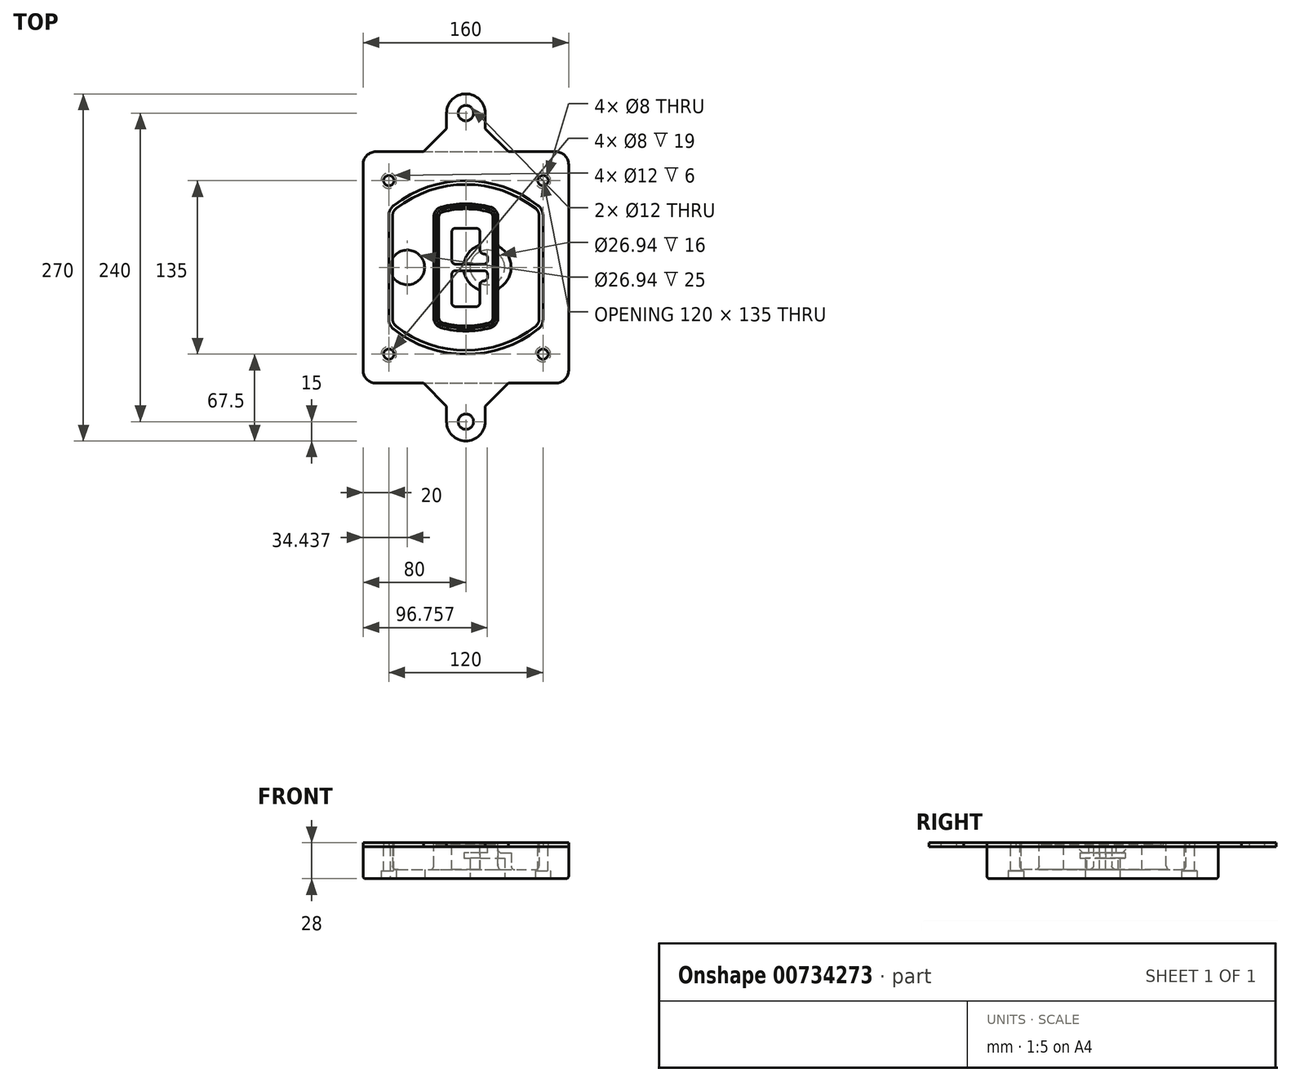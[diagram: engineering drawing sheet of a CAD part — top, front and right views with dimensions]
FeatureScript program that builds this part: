
annotation { "Feature Type Name" : "Feature", "Feature Type Description" : "" }
export const myFeature = defineFeature(function(context is Context, id is Id, definition is map)
    precondition{}
    {
        {
            var Q0;
            Q0=qCreatedBy(makeId("Top.planeOp"),FACE);
            var sketch = newSketch(context, id + "F0", { "sketchPlane" : qUnion([Q0])});
            skPoint(sketch, "E0.rect.middle", {"position": v(0, 0) * mm});
            skLineSegment(sketch, "E1.bottom", {"start": v(-70, -90) * mm, "end": v(70, -90) * mm});
            skLineSegment(sketch, "E1.top", {"start": v(-70, 90) * mm, "end": v(70, 90) * mm});
            skLineSegment(sketch, "E1.left", {"start": v(-80, -80) * mm, "end": v(-80, 80) * mm});
            skLineSegment(sketch, "E1.right", {"start": v(80, -80) * mm, "end": v(80, 80) * mm});
            skLineSegment(sketch, "E2", {"start": v(-80, 90) * mm, "end": v(80, -90) * mm, "construction": true});
            skLineSegment(sketch, "E3", {"start": v(80, 90) * mm, "end": v(-80, -90) * mm, "construction": true});
            skCircle(sketch, "E4", {"center": v(-60, 67.5) * mm, "radius": 4 * mm});
            skCircle(sketch, "E5", {"center": v(60, 67.5) * mm, "radius": 4 * mm});
            skCircle(sketch, "E6", {"center": v(60, -67.5) * mm, "radius": 4 * mm});
            skCircle(sketch, "E7", {"center": v(-60, -67.5) * mm, "radius": 4 * mm});
            skLineSegment(sketch, "E8", {"start": v(-60, 67.5) * mm, "end": v(60, 67.5) * mm, "construction": true});
            skLineSegment(sketch, "E9", {"start": v(60, 67.5) * mm, "end": v(60, -67.5) * mm, "construction": true});
            skLineSegment(sketch, "E10", {"start": v(60, -67.5) * mm, "end": v(-60, -67.5) * mm, "construction": true});
            skLineSegment(sketch, "E11", {"start": v(-60, -67.5) * mm, "end": v(-60, 67.5) * mm, "construction": true});
            skLineSegment(sketch, "E12", {"start": v(-60, 40.3) * mm, "end": v(-60, -40.3) * mm});
            skLineSegment(sketch, "E13", {"start": v(60, 40.3) * mm, "end": v(60, -40.3) * mm});
            skArc(sketch, "E14", {"start": v(56.15, 48.18) * mm, "mid": v(0, 67.5) * mm, "end": v(-56.15, 48.18) * mm});
            skArc(sketch, "E15", {"start": v(-56.15, -48.18) * mm, "mid": v(0, -67.5) * mm, "end": v(56.15, -48.18) * mm});
            skLineSegment(sketch, "E16", {"start": v(-60, 0) * mm, "end": v(60, 0) * mm, "construction": true});
            skPoint(sketch, "E17.visualSharp", {"position": v(-60, -45) * mm});
            skArc(sketch, "E17.filletArc", {"start": v(-60, -40.3) * mm, "mid": v(-58.99, -44.68) * mm, "end": v(-56.15, -48.18) * mm});
            skPoint(sketch, "E18.visualSharp", {"position": v(-60, 45) * mm});
            skArc(sketch, "E18.filletArc", {"start": v(-56.15, 48.18) * mm, "mid": v(-58.99, 44.68) * mm, "end": v(-60, 40.3) * mm});
            skPoint(sketch, "E19.visualSharp", {"position": v(60, 45) * mm});
            skArc(sketch, "E19.filletArc", {"start": v(60, 40.3) * mm, "mid": v(58.99, 44.68) * mm, "end": v(56.15, 48.18) * mm});
            skPoint(sketch, "E20.visualSharp", {"position": v(60, -45) * mm});
            skArc(sketch, "E20.filletArc", {"start": v(56.15, -48.18) * mm, "mid": v(58.99, -44.68) * mm, "end": v(60, -40.3) * mm});
            skPoint(sketch, "E21.visualSharp", {"position": v(-80, 90) * mm});
            skArc(sketch, "E21.filletArc", {"start": v(-70, 90) * mm, "mid": v(-77.07, 87.07) * mm, "end": v(-80, 80) * mm});
            skPoint(sketch, "E22.visualSharp", {"position": v(80, 90) * mm});
            skArc(sketch, "E22.filletArc", {"start": v(80, 80) * mm, "mid": v(77.07, 87.07) * mm, "end": v(70, 90) * mm});
            skPoint(sketch, "E23.visualSharp", {"position": v(80, -90) * mm});
            skArc(sketch, "E23.filletArc", {"start": v(70, -90) * mm, "mid": v(77.07, -87.07) * mm, "end": v(80, -80) * mm});
            skPoint(sketch, "E24.visualSharp", {"position": v(-80, -90) * mm});
            skArc(sketch, "E24.filletArc", {"start": v(-80, -80) * mm, "mid": v(-77.07, -87.07) * mm, "end": v(-70, -90) * mm});
            skArc(sketch, "E25.0", {"start": v(57, 40.3) * mm, "mid": v(56.3, 43.36) * mm, "end": v(54.3, 45.81) * mm});
            skLineSegment(sketch, "E25.1", {"start": v(57, 40.3) * mm, "end": v(57, -40.3) * mm});
            skArc(sketch, "E25.2", {"start": v(54.3, -45.81) * mm, "mid": v(56.3, -43.36) * mm, "end": v(57, -40.3) * mm});
            skArc(sketch, "E25.3", {"start": v(-54.3, -45.81) * mm, "mid": v(0, -64.5) * mm, "end": v(54.3, -45.81) * mm});
            skArc(sketch, "E25.4", {"start": v(-57, -40.3) * mm, "mid": v(-56.3, -43.36) * mm, "end": v(-54.3, -45.81) * mm});
            skArc(sketch, "E25.5", {"start": v(54.3, 45.81) * mm, "mid": v(0, 64.5) * mm, "end": v(-54.3, 45.81) * mm});
            skLineSegment(sketch, "E25.6", {"start": v(-57, 40.3) * mm, "end": v(-57, -40.3) * mm});
            skArc(sketch, "E25.7", {"start": v(-54.3, 45.81) * mm, "mid": v(-56.3, 43.36) * mm, "end": v(-57, 40.3) * mm});
            skArc(sketch, "E26.0", {"start": v(-58.62, 51.33) * mm, "mid": v(-62.58, 46.43) * mm, "end": v(-64, 40.3) * mm});
            skArc(sketch, "E26.1", {"start": v(58.62, 51.33) * mm, "mid": v(0, 71.5) * mm, "end": v(-58.62, 51.33) * mm});
            skArc(sketch, "E26.2", {"start": v(64, 40.3) * mm, "mid": v(62.58, 46.43) * mm, "end": v(58.62, 51.33) * mm});
            skLineSegment(sketch, "E26.3", {"start": v(64, 40.3) * mm, "end": v(64, -40.3) * mm});
            skArc(sketch, "E26.4", {"start": v(58.62, -51.33) * mm, "mid": v(62.58, -46.43) * mm, "end": v(64, -40.3) * mm});
            skLineSegment(sketch, "E26.5", {"start": v(-64, 40.3) * mm, "end": v(-64, -40.3) * mm});
            skArc(sketch, "E26.6", {"start": v(-58.62, -51.33) * mm, "mid": v(0, -71.5) * mm, "end": v(58.62, -51.33) * mm});
            skArc(sketch, "E26.7", {"start": v(-64, -40.3) * mm, "mid": v(-62.58, -46.43) * mm, "end": v(-58.62, -51.33) * mm});
            skSolve(sketch);
        }
        {
            var Q0;
            Q0=makeQuery(id+"F0.imprint","IMPRINT",FACE,{"disambiguationData":[TD([[makeQuery(id+"F0.imprint","IMPRINT",EDGE,{"derivedFrom":sQuery(id+"F0.wireOp",EDGE,"E1.bottom")}),1.0]])]});
            var Q1;
            Q1=makeQuery(id+"F0.imprint","IMPRINT",FACE,{"disambiguationData":[TD([[makeQuery(id+"F0.imprint","IMPRINT",EDGE,{"derivedFrom":sQuery(id+"F0.wireOp",EDGE,"E12")}),1.0]])]});
            var Q2;
            Q2=makeQuery(id+"F0.imprint","IMPRINT",FACE,{"disambiguationData":[TD([[makeQuery(id+"F0.imprint","IMPRINT",EDGE,{"derivedFrom":sQuery(id+"F0.wireOp",EDGE,"E25.0")}),1.0]])]});
            var Q3;
            Q3=makeQuery(id+"F0.imprint","IMPRINT",FACE,{"disambiguationData":[TD([[makeQuery(id+"F0.imprint","IMPRINT",EDGE,{"derivedFrom":sQuery(id+"F0.wireOp",EDGE,"E12")}),-1.0]])]});
            extrude(context, id + "F1", {"entities" : qUnion([Q0, Q1, Q2, Q3]), "oppositeDirection" : true, "depth" : 25 * mm});
        }
        {
            var Q0;
            Q0=makeQuery(id+"F0.imprint","IMPRINT",FACE,{"disambiguationData":[TD([[makeQuery(id+"F0.imprint","IMPRINT",EDGE,{"derivedFrom":sQuery(id+"F0.wireOp",EDGE,"E12")}),1.0]])]});
            extrude(context, id + "F2", {"entities" : qUnion([Q0]), "operationType" : NewBodyOperationType.ADD, "depth" : 3 * mm});
        }
        {
            var Q0;
            Q0=makeQuery(id+"F0.imprint","IMPRINT",FACE,{"disambiguationData":[TD([[makeQuery(id+"F0.imprint","IMPRINT",EDGE,{"derivedFrom":sQuery(id+"F0.wireOp",EDGE,"E25.0")}),1.0]])]});
            extrude(context, id + "F3", {"entities" : qUnion([Q0]), "operationType" : NewBodyOperationType.REMOVE, "oppositeDirection" : true, "depth" : 18 * mm});
        }
        {
            var Q0;
            Q0=makeQuery(id+"F2.opExtrude","CAP_FACE",FACE,{"disambiguationData":[OSD([sQuery(id+"F0.wireOp",EDGE,"E12"),sQuery(id+"F0.wireOp",EDGE,"E13"),sQuery(id+"F0.wireOp",EDGE,"E14"),sQuery(id+"F0.wireOp",EDGE,"E15"),sQuery(id+"F0.wireOp",EDGE,"E17.filletArc"),sQuery(id+"F0.wireOp",EDGE,"E18.filletArc"),sQuery(id+"F0.wireOp",EDGE,"E19.filletArc"),sQuery(id+"F0.wireOp",EDGE,"E20.filletArc"),sQuery(id+"F0.wireOp",EDGE,"E25.0"),sQuery(id+"F0.wireOp",EDGE,"E25.1"),sQuery(id+"F0.wireOp",EDGE,"E25.2"),sQuery(id+"F0.wireOp",EDGE,"E25.3"),sQuery(id+"F0.wireOp",EDGE,"E25.4"),sQuery(id+"F0.wireOp",EDGE,"E25.5"),sQuery(id+"F0.wireOp",EDGE,"E25.6"),sQuery(id+"F0.wireOp",EDGE,"E25.7")])],"isStart":false});
            var sketch = newSketch(context, id + "F4", { "sketchPlane" : qUnion([Q0])});
            skArc(sketch, "E27.0", {"start": v(-19.08, -46.97) * mm, "mid": v(0, -49.5) * mm, "end": v(19.08, -46.97) * mm});
            skArc(sketch, "E28.0", {"start": v(19.08, 46.97) * mm, "mid": v(0, 49.5) * mm, "end": v(-19.08, 46.97) * mm});
            skLineSegment(sketch, "E29", {"start": v(-25, 39.25) * mm, "end": v(-25, -39.25) * mm});
            skLineSegment(sketch, "E30", {"start": v(25, 39.25) * mm, "end": v(25, -39.25) * mm});
            skLineSegment(sketch, "E31", {"start": v(-25, 45.1) * mm, "end": v(25, 45.1) * mm, "construction": true});
            skLineSegment(sketch, "E32", {"start": v(-25, -45.1) * mm, "end": v(25, -45.1) * mm, "construction": true});
            skPoint(sketch, "E33.visualSharp", {"position": v(-25, 45.1) * mm});
            skArc(sketch, "E33.filletArc", {"start": v(-19.08, 46.97) * mm, "mid": v(-23.35, 44.11) * mm, "end": v(-25, 39.25) * mm});
            skPoint(sketch, "E34.visualSharp", {"position": v(25, 45.1) * mm});
            skArc(sketch, "E34.filletArc", {"start": v(25, 39.25) * mm, "mid": v(23.35, 44.11) * mm, "end": v(19.08, 46.97) * mm});
            skPoint(sketch, "E35.visualSharp", {"position": v(25, -45.1) * mm});
            skArc(sketch, "E35.filletArc", {"start": v(19.08, -46.97) * mm, "mid": v(23.35, -44.11) * mm, "end": v(25, -39.25) * mm});
            skPoint(sketch, "E36.visualSharp", {"position": v(-25, -45.1) * mm});
            skArc(sketch, "E36.filletArc", {"start": v(-25, -39.25) * mm, "mid": v(-23.35, -44.11) * mm, "end": v(-19.08, -46.97) * mm});
            skArc(sketch, "E37.0", {"start": v(54.3, 45.81) * mm, "mid": v(0, 64.5) * mm, "end": v(-54.3, 45.81) * mm});
            skArc(sketch, "E37.1", {"start": v(-54.3, 45.81) * mm, "mid": v(-56.3, 43.36) * mm, "end": v(-57, 40.3) * mm});
            skLineSegment(sketch, "E37.2", {"start": v(-57, 40.3) * mm, "end": v(-57, -40.3) * mm});
            skArc(sketch, "E37.3", {"start": v(-57, -40.3) * mm, "mid": v(-56.3, -43.36) * mm, "end": v(-54.3, -45.81) * mm});
            skArc(sketch, "E37.4", {"start": v(-54.3, -45.81) * mm, "mid": v(0, -64.5) * mm, "end": v(54.3, -45.81) * mm});
            skArc(sketch, "E37.5", {"start": v(54.3, -45.81) * mm, "mid": v(56.3, -43.36) * mm, "end": v(57, -40.3) * mm});
            skLineSegment(sketch, "E37.6", {"start": v(57, 40.3) * mm, "end": v(57, -40.3) * mm});
            skArc(sketch, "E37.7", {"start": v(57, 40.3) * mm, "mid": v(56.3, 43.36) * mm, "end": v(54.3, 45.81) * mm});
            skLineSegment(sketch, "E38.0", {"start": v(23, 39.25) * mm, "end": v(23, -39.25) * mm});
            skArc(sketch, "E38.1", {"start": v(18.56, -45.04) * mm, "mid": v(21.76, -42.9) * mm, "end": v(23, -39.25) * mm});
            skArc(sketch, "E38.2", {"start": v(-18.56, -45.04) * mm, "mid": v(0, -47.5) * mm, "end": v(18.56, -45.04) * mm});
            skArc(sketch, "E38.3", {"start": v(-23, -39.25) * mm, "mid": v(-21.76, -42.9) * mm, "end": v(-18.56, -45.04) * mm});
            skLineSegment(sketch, "E38.4", {"start": v(-23, 39.25) * mm, "end": v(-23, -39.25) * mm});
            skArc(sketch, "E38.5", {"start": v(23, 39.25) * mm, "mid": v(21.76, 42.9) * mm, "end": v(18.56, 45.04) * mm});
            skArc(sketch, "E38.6", {"start": v(-18.56, 45.04) * mm, "mid": v(-21.76, 42.9) * mm, "end": v(-23, 39.25) * mm});
            skArc(sketch, "E38.7", {"start": v(18.56, 45.04) * mm, "mid": v(0, 47.5) * mm, "end": v(-18.56, 45.04) * mm});
            skArc(sketch, "E39.0", {"start": v(21, 39.25) * mm, "mid": v(20.18, 41.68) * mm, "end": v(18.04, 43.1) * mm});
            skLineSegment(sketch, "E39.1", {"start": v(21, 39.25) * mm, "end": v(21, -39.25) * mm});
            skArc(sketch, "E39.2", {"start": v(18.04, -43.1) * mm, "mid": v(20.18, -41.68) * mm, "end": v(21, -39.25) * mm});
            skArc(sketch, "E39.3", {"start": v(-18.04, -43.1) * mm, "mid": v(0, -45.5) * mm, "end": v(18.04, -43.1) * mm});
            skArc(sketch, "E39.4", {"start": v(-21, -39.25) * mm, "mid": v(-20.18, -41.68) * mm, "end": v(-18.04, -43.1) * mm});
            skArc(sketch, "E39.5", {"start": v(18.04, 43.1) * mm, "mid": v(0, 45.5) * mm, "end": v(-18.04, 43.1) * mm});
            skLineSegment(sketch, "E39.6", {"start": v(-21, 39.25) * mm, "end": v(-21, -39.25) * mm});
            skArc(sketch, "E39.7", {"start": v(-18.04, 43.1) * mm, "mid": v(-20.18, 41.68) * mm, "end": v(-21, 39.25) * mm});
            skLineSegment(sketch, "E40", {"start": v(-25, 0) * mm, "end": v(25, 0) * mm, "construction": true});
            skLineSegment(sketch, "E41", {"start": v(-11, 5.5) * mm, "end": v(-11, 27.5) * mm});
            skLineSegment(sketch, "E42", {"start": v(-8, 30.5) * mm, "end": v(8, 30.5) * mm});
            skLineSegment(sketch, "E43", {"start": v(11, 27.5) * mm, "end": v(11, 13.5) * mm});
            skLineSegment(sketch, "E44", {"start": v(14, 10.5) * mm, "end": v(14, 10.5) * mm});
            skLineSegment(sketch, "E45", {"start": v(17, 7.5) * mm, "end": v(17, 5.5) * mm});
            skLineSegment(sketch, "E46", {"start": v(14, 2.5) * mm, "end": v(-8, 2.5) * mm});
            skPoint(sketch, "E47.visualSharp", {"position": v(-11, 30.5) * mm});
            skArc(sketch, "E47.filletArc", {"start": v(-8, 30.5) * mm, "mid": v(-10.12, 29.62) * mm, "end": v(-11, 27.5) * mm});
            skPoint(sketch, "E48.visualSharp", {"position": v(11, 30.5) * mm});
            skArc(sketch, "E48.filletArc", {"start": v(11, 27.5) * mm, "mid": v(10.12, 29.62) * mm, "end": v(8, 30.5) * mm});
            skPoint(sketch, "E49.visualSharp", {"position": v(11, 10.5) * mm});
            skArc(sketch, "E49.filletArc", {"start": v(11, 13.5) * mm, "mid": v(11.88, 11.38) * mm, "end": v(14, 10.5) * mm});
            skPoint(sketch, "E50.visualSharp", {"position": v(17, 10.5) * mm});
            skArc(sketch, "E50.filletArc", {"start": v(17, 7.5) * mm, "mid": v(16.12, 9.62) * mm, "end": v(14, 10.5) * mm});
            skPoint(sketch, "E51.visualSharp", {"position": v(17, 2.5) * mm});
            skArc(sketch, "E51.filletArc", {"start": v(14, 2.5) * mm, "mid": v(16.12, 3.38) * mm, "end": v(17, 5.5) * mm});
            skPoint(sketch, "E52.visualSharp", {"position": v(-11, 2.5) * mm});
            skArc(sketch, "E52.filletArc", {"start": v(-11, 5.5) * mm, "mid": v(-10.12, 3.38) * mm, "end": v(-8, 2.5) * mm});
            skLineSegment(sketch, "E53.0.MirrorCS", {"start": v(14, -2.5) * mm, "end": v(-8, -2.5) * mm});
            skArc(sketch, "E54.0.MirrorCS", {"start": v(-11, -5.5) * mm, "mid": v(-10.12, -3.38) * mm, "end": v(-8, -2.5) * mm});
            skLineSegment(sketch, "E55.0.MirrorCS", {"start": v(-11, -5.5) * mm, "end": v(-11, -27.5) * mm});
            skArc(sketch, "E56.0.MirrorCS", {"start": v(-8, -30.5) * mm, "mid": v(-10.12, -29.62) * mm, "end": v(-11, -27.5) * mm});
            skLineSegment(sketch, "E57.0.MirrorCS", {"start": v(-8, -30.5) * mm, "end": v(8, -30.5) * mm});
            skArc(sketch, "E58.0.MirrorCS", {"start": v(11, -27.5) * mm, "mid": v(10.12, -29.62) * mm, "end": v(8, -30.5) * mm});
            skLineSegment(sketch, "E59.0.MirrorCS", {"start": v(11, -27.5) * mm, "end": v(11, -13.5) * mm});
            skArc(sketch, "E60.0.MirrorCS", {"start": v(11, -13.5) * mm, "mid": v(11.88, -11.38) * mm, "end": v(14, -10.5) * mm});
            skArc(sketch, "E61.0.MirrorCS", {"start": v(17, -7.5) * mm, "mid": v(16.12, -9.62) * mm, "end": v(14, -10.5) * mm});
            skLineSegment(sketch, "E62.0.MirrorCS", {"start": v(17, -7.5) * mm, "end": v(17, -5.5) * mm});
            skArc(sketch, "E63.0.MirrorCS", {"start": v(14, -2.5) * mm, "mid": v(16.12, -3.38) * mm, "end": v(17, -5.5) * mm});
            skSolve(sketch);
        }
        {
            var Q0;
            Q0=makeQuery(id+"F4.imprint","IMPRINT",FACE,{"disambiguationData":[TD([[makeQuery(id+"F4.imprint","IMPRINT",EDGE,{"derivedFrom":sQuery(id+"F4.wireOp",EDGE,"E27.0")}),1.0]])]});
            var Q1;
            Q1=makeQuery(id+"F4.imprint","IMPRINT",FACE,{"disambiguationData":[TD([[makeQuery(id+"F4.imprint","IMPRINT",EDGE,{"derivedFrom":sQuery(id+"F4.wireOp",EDGE,"E38.0")}),-1.0]])]});
            var Q2;
            Q2=makeQuery(id+"F4.imprint","IMPRINT",FACE,{"disambiguationData":[TD([[makeQuery(id+"F4.imprint","IMPRINT",EDGE,{"derivedFrom":sQuery(id+"F4.wireOp",EDGE,"E39.0")}),1.0]])]});
            extrude(context, id + "F5", {"entities" : qUnion([Q0, Q1, Q2]), "operationType" : NewBodyOperationType.ADD, "endBound" : BoundingType.UP_TO_NEXT, "oppositeDirection" : true, "depth" : 25 * mm});
        }
        {
            var Q0;
            Q0=makeQuery(id+"F4.imprint","IMPRINT",FACE,{"disambiguationData":[TD([[makeQuery(id+"F4.imprint","IMPRINT",EDGE,{"derivedFrom":sQuery(id+"F4.wireOp",EDGE,"E38.0")}),-1.0]])]});
            extrude(context, id + "F6", {"entities" : qUnion([Q0]), "operationType" : NewBodyOperationType.REMOVE, "oppositeDirection" : true, "depth" : 2 * mm});
        }
        {
            var Q0;
            Q0=makeQuery(id+"F1.opExtrude","CAP_FACE",FACE,{"disambiguationData":[OSD([sQuery(id+"F0.wireOp",EDGE,"E1.bottom"),sQuery(id+"F0.wireOp",EDGE,"E1.top"),sQuery(id+"F0.wireOp",EDGE,"E1.left"),sQuery(id+"F0.wireOp",EDGE,"E1.right"),sQuery(id+"F0.wireOp",EDGE,"E4"),sQuery(id+"F0.wireOp",EDGE,"E5"),sQuery(id+"F0.wireOp",EDGE,"E6"),sQuery(id+"F0.wireOp",EDGE,"E7"),sQuery(id+"F0.wireOp",EDGE,"E21.filletArc"),sQuery(id+"F0.wireOp",EDGE,"E22.filletArc"),sQuery(id+"F0.wireOp",EDGE,"E23.filletArc"),sQuery(id+"F0.wireOp",EDGE,"E24.filletArc")])],"isStart":false});
            var sketch = newSketch(context, id + "F7", { "sketchPlane" : qUnion([Q0])});
            skCircle(sketch, "E64", {"center": v(16.76, 0) * mm, "radius": 13.47 * mm});
            skCircle(sketch, "E65", {"center": v(-45.56, 0) * mm, "radius": 13.47 * mm});
            skLineSegment(sketch, "E66", {"start": v(80, 0) * mm, "end": v(-80, 0) * mm});
            skCircle(sketch, "E67", {"center": v(16.76, 0) * mm, "radius": 18.47 * mm});
            skCircle(sketch, "E68", {"center": v(60, -67.5) * mm, "radius": 6 * mm});
            skCircle(sketch, "E69", {"center": v(-60, -67.5) * mm, "radius": 6 * mm});
            skCircle(sketch, "E70", {"center": v(-60, 67.5) * mm, "radius": 6 * mm});
            skCircle(sketch, "E71", {"center": v(60, 67.5) * mm, "radius": 6 * mm});
            skSolve(sketch);
        }
        {
            var Q0;
            {var subQ1=sQuery(id+"F7.wireOp",EDGE,"E66");var subQ4=sQuery(id+"F7.wireOp",EDGE,"E64");var subQ6=makeQuery(id+"F7.imprint","INTERSECT",VERTEX,{"disambiguationData":[OD(0.0)],"derivedFrom":[subQ4,subQ1]});Q0=makeQuery(id+"F7.imprint","IMPRINT",FACE,{"disambiguationData":[TD([[makeQuery(id+"F7.imprint","IMPRINT",EDGE,{"disambiguationData":[TD([[subQ6,-1.0]])],"derivedFrom":subQ4}),-1.0]])]});}
            var Q1;
            {var subQ0=sQuery(id+"F7.wireOp",EDGE,"E66");var subQ1=sQuery(id+"F7.wireOp",EDGE,"E64");var subQ3=makeQuery(id+"F7.imprint","INTERSECT",VERTEX,{"disambiguationData":[OD(0.0)],"derivedFrom":[subQ1,subQ0]});Q1=makeQuery(id+"F7.imprint","IMPRINT",FACE,{"disambiguationData":[TD([[makeQuery(id+"F7.imprint","IMPRINT",EDGE,{"disambiguationData":[TD([[subQ3,-1.0]])],"derivedFrom":subQ1}),1.0]])]});}
            var Q2;
            {var subQ0=sQuery(id+"F7.wireOp",EDGE,"E66");var subQ1=sQuery(id+"F7.wireOp",EDGE,"E64");var subQ3=makeQuery(id+"F7.imprint","INTERSECT",VERTEX,{"disambiguationData":[OD(0.0)],"derivedFrom":[subQ1,subQ0]});Q2=makeQuery(id+"F7.imprint","IMPRINT",FACE,{"disambiguationData":[TD([[makeQuery(id+"F7.imprint","IMPRINT",EDGE,{"disambiguationData":[TD([[subQ3,1.0]])],"derivedFrom":subQ1}),1.0]])]});}
            var Q3;
            {var subQ1=sQuery(id+"F7.wireOp",EDGE,"E66");var subQ4=sQuery(id+"F7.wireOp",EDGE,"E64");var subQ6=makeQuery(id+"F7.imprint","INTERSECT",VERTEX,{"disambiguationData":[OD(0.0)],"derivedFrom":[subQ4,subQ1]});Q3=makeQuery(id+"F7.imprint","IMPRINT",FACE,{"disambiguationData":[TD([[makeQuery(id+"F7.imprint","IMPRINT",EDGE,{"disambiguationData":[TD([[subQ6,1.0]])],"derivedFrom":subQ4}),-1.0]])]});}
            extrude(context, id + "F8", {"entities" : qUnion([Q0, Q1, Q2, Q3]), "operationType" : NewBodyOperationType.ADD, "oppositeDirection" : true, "depth" : 20 * mm});
        }
        {
            var Q0;
            {var subQ0=sQuery(id+"F7.wireOp",EDGE,"E66");var subQ1=sQuery(id+"F7.wireOp",EDGE,"E64");var subQ3=makeQuery(id+"F7.imprint","INTERSECT",VERTEX,{"disambiguationData":[OD(0.0)],"derivedFrom":[subQ1,subQ0]});Q0=makeQuery(id+"F7.imprint","IMPRINT",FACE,{"disambiguationData":[TD([[makeQuery(id+"F7.imprint","IMPRINT",EDGE,{"disambiguationData":[TD([[subQ3,-1.0]])],"derivedFrom":subQ1}),1.0]])]});}
            var Q1;
            {var subQ0=sQuery(id+"F7.wireOp",EDGE,"E66");var subQ1=sQuery(id+"F7.wireOp",EDGE,"E64");var subQ3=makeQuery(id+"F7.imprint","INTERSECT",VERTEX,{"disambiguationData":[OD(0.0)],"derivedFrom":[subQ1,subQ0]});Q1=makeQuery(id+"F7.imprint","IMPRINT",FACE,{"disambiguationData":[TD([[makeQuery(id+"F7.imprint","IMPRINT",EDGE,{"disambiguationData":[TD([[subQ3,1.0]])],"derivedFrom":subQ1}),1.0]])]});}
            extrude(context, id + "F9", {"entities" : qUnion([Q0, Q1]), "operationType" : NewBodyOperationType.REMOVE, "oppositeDirection" : true, "depth" : 16 * mm});
        }
        {
            var Q0;
            {var subQ0=sQuery(id+"F7.wireOp",EDGE,"E66");var subQ1=sQuery(id+"F7.wireOp",EDGE,"E65");var subQ3=makeQuery(id+"F7.imprint","INTERSECT",VERTEX,{"disambiguationData":[OD(0.0)],"derivedFrom":[subQ1,subQ0]});Q0=makeQuery(id+"F7.imprint","IMPRINT",FACE,{"disambiguationData":[TD([[makeQuery(id+"F7.imprint","IMPRINT",EDGE,{"disambiguationData":[TD([[subQ3,-1.0]])],"derivedFrom":subQ1}),1.0]])]});}
            var Q1;
            {var subQ0=sQuery(id+"F7.wireOp",EDGE,"E66");var subQ1=sQuery(id+"F7.wireOp",EDGE,"E65");var subQ3=makeQuery(id+"F7.imprint","INTERSECT",VERTEX,{"disambiguationData":[OD(0.0)],"derivedFrom":[subQ1,subQ0]});Q1=makeQuery(id+"F7.imprint","IMPRINT",FACE,{"disambiguationData":[TD([[makeQuery(id+"F7.imprint","IMPRINT",EDGE,{"disambiguationData":[TD([[subQ3,1.0]])],"derivedFrom":subQ1}),1.0]])]});}
            extrude(context, id + "F10", {"entities" : qUnion([Q0, Q1]), "operationType" : NewBodyOperationType.REMOVE, "oppositeDirection" : true, "depth" : 25 * mm});
        }
        {
            var Q0;
            Q0=makeQuery(id+"F7.imprint","IMPRINT",FACE,{"disambiguationData":[TD([[makeQuery(id+"F7.imprint","IMPRINT",EDGE,{"derivedFrom":sQuery(id+"F7.wireOp",EDGE,"E68")}),1.0]])]});
            var Q1;
            Q1=makeQuery(id+"F7.imprint","IMPRINT",FACE,{"disambiguationData":[TD([[makeQuery(id+"F7.imprint","IMPRINT",EDGE,{"derivedFrom":makeQuery(id+"F1.opExtrude","CAP_EDGE",EDGE,{"disambiguationData":[OSD([sQuery(id+"F0.wireOp",EDGE,"E5")])],"isStart":false})}),-1.0]])]});
            var Q2;
            Q2=makeQuery(id+"F7.imprint","IMPRINT",FACE,{"disambiguationData":[TD([[makeQuery(id+"F7.imprint","IMPRINT",EDGE,{"derivedFrom":sQuery(id+"F7.wireOp",EDGE,"E69")}),1.0]])]});
            var Q3;
            Q3=makeQuery(id+"F7.imprint","IMPRINT",FACE,{"disambiguationData":[TD([[makeQuery(id+"F7.imprint","IMPRINT",EDGE,{"derivedFrom":makeQuery(id+"F1.opExtrude","CAP_EDGE",EDGE,{"disambiguationData":[OSD([sQuery(id+"F0.wireOp",EDGE,"E4")])],"isStart":false})}),-1.0]])]});
            var Q4;
            Q4=makeQuery(id+"F7.imprint","IMPRINT",FACE,{"disambiguationData":[TD([[makeQuery(id+"F7.imprint","IMPRINT",EDGE,{"derivedFrom":sQuery(id+"F7.wireOp",EDGE,"E70")}),1.0]])]});
            var Q5;
            Q5=makeQuery(id+"F7.imprint","IMPRINT",FACE,{"disambiguationData":[TD([[makeQuery(id+"F7.imprint","IMPRINT",EDGE,{"derivedFrom":makeQuery(id+"F1.opExtrude","CAP_EDGE",EDGE,{"disambiguationData":[OSD([sQuery(id+"F0.wireOp",EDGE,"E7")])],"isStart":false})}),-1.0]])]});
            var Q6;
            Q6=makeQuery(id+"F7.imprint","IMPRINT",FACE,{"disambiguationData":[TD([[makeQuery(id+"F7.imprint","IMPRINT",EDGE,{"derivedFrom":sQuery(id+"F7.wireOp",EDGE,"E71")}),1.0]])]});
            var Q7;
            Q7=makeQuery(id+"F7.imprint","IMPRINT",FACE,{"disambiguationData":[TD([[makeQuery(id+"F7.imprint","IMPRINT",EDGE,{"derivedFrom":makeQuery(id+"F1.opExtrude","CAP_EDGE",EDGE,{"disambiguationData":[OSD([sQuery(id+"F0.wireOp",EDGE,"E6")])],"isStart":false})}),-1.0]])]});
            extrude(context, id + "F11", {"entities" : qUnion([Q0, Q1, Q2, Q3, Q4, Q5, Q6, Q7]), "operationType" : NewBodyOperationType.REMOVE, "oppositeDirection" : true, "depth" : 6 * mm});
        }
        {
            var Q0;
            Q0=makeQuery(id+"F9.boolean.opBoolean","COPY",FACE,{"derivedFrom":makeQuery(id+"F9.opExtrude","CAP_FACE",FACE,{"disambiguationData":[OSD([sQuery(id+"F7.wireOp",EDGE,"E64")])],"isStart":false})});
            var sketch = newSketch(context, id + "F12", { "sketchPlane" : qUnion([Q0])});
            skArc(sketch, "E72.0", {"start": v(11, 17.55) * mm, "mid": v(2.57, 11.82) * mm, "end": v(-1.54, 2.5) * mm});
            skArc(sketch, "E72.1", {"start": v(-1.54, -2.5) * mm, "mid": v(2.57, -11.82) * mm, "end": v(11, -17.55) * mm});
            skLineSegment(sketch, "E73", {"start": v(-1.54, -2.5) * mm, "end": v(14, -2.5) * mm});
            skLineSegment(sketch, "E74.0", {"start": v(14, 2.5) * mm, "end": v(-1.54, 2.5) * mm});
            skArc(sketch, "E74.1", {"start": v(14, 2.5) * mm, "mid": v(16.12, 3.38) * mm, "end": v(17, 5.5) * mm});
            skLineSegment(sketch, "E74.2", {"start": v(17, 7.5) * mm, "end": v(17, 5.5) * mm});
            skArc(sketch, "E74.3", {"start": v(17, 7.5) * mm, "mid": v(16.12, 9.62) * mm, "end": v(14, 10.5) * mm});
            skArc(sketch, "E74.4", {"start": v(11, 13.5) * mm, "mid": v(11.88, 11.38) * mm, "end": v(14, 10.5) * mm});
            skLineSegment(sketch, "E74.5", {"start": v(11, 17.55) * mm, "end": v(11, 13.5) * mm});
            skLineSegment(sketch, "E74.7", {"start": v(14, -2.5) * mm, "end": v(-1.54, -2.5) * mm});
            skArc(sketch, "E74.8", {"start": v(14, -2.5) * mm, "mid": v(16.12, -3.38) * mm, "end": v(17, -5.5) * mm});
            skLineSegment(sketch, "E74.9", {"start": v(17, -7.5) * mm, "end": v(17, -5.5) * mm});
            skArc(sketch, "E74.10", {"start": v(17, -7.5) * mm, "mid": v(16.12, -9.62) * mm, "end": v(14, -10.5) * mm});
            skArc(sketch, "E74.11", {"start": v(11, -13.5) * mm, "mid": v(11.88, -11.38) * mm, "end": v(14, -10.5) * mm});
            skLineSegment(sketch, "E74.12", {"start": v(11, -17.55) * mm, "end": v(11, -13.5) * mm});
            skPoint(sketch, "E75.orphan", {"position": v(11, -27.5) * mm});
            skPoint(sketch, "E76.orphan", {"position": v(-8, -2.5) * mm});
            skPoint(sketch, "E77.orphan", {"position": v(-8, 2.5) * mm});
            skPoint(sketch, "E78.orphan", {"position": v(11, 27.5) * mm});
            skSolve(sketch);
        }
        {
            var Q0;
            {var subQ7=sQuery(id+"F12.wireOp",EDGE,"E72.0");var subQ14=sQuery(id+"F12.wireOp",EDGE,"E72.1");var subQ16=sQuery(id+"F12.wireOp",EDGE,"E74.1");var subQ18=sQuery(id+"F12.wireOp",EDGE,"E74.8");Q0=qUnion([makeQuery(id+"F12.imprint","IMPRINT",FACE,{"disambiguationData":[TD([[makeQuery(id+"F12.imprint","IMPRINT",EDGE,{"derivedFrom":subQ7}),1.0]])]}),makeQuery(id+"F12.imprint","IMPRINT",FACE,{"disambiguationData":[TD([[makeQuery(id+"F12.imprint","IMPRINT",EDGE,{"derivedFrom":subQ14}),1.0]])]}),makeQuery(id+"F12.imprint","IMPRINT",FACE,{"disambiguationData":[TD([[makeQuery(id+"F12.imprint","IMPRINT",EDGE,{"derivedFrom":subQ16}),1.0]])]}),makeQuery(id+"F12.imprint","IMPRINT",FACE,{"disambiguationData":[TD([[makeQuery(id+"F12.imprint","IMPRINT",EDGE,{"derivedFrom":subQ18}),-1.0]])]})]);}
            var Q1;
            Q1=makeQuery(id+"F5.boolean.opBoolean","SPLIT",FACE,{"disambiguationData":[TD([makeQuery(id+"F5.opExtrude","SWEPT_FACE",FACE,{"disambiguationData":[OSD([sQuery(id+"F4.wireOp",EDGE,"E41")])]})])],"derivedFrom":makeQuery(id+"F3.boolean.opBoolean","COPY",FACE,{"derivedFrom":makeQuery(id+"F3.opExtrude","CAP_FACE",FACE,{"disambiguationData":[OSD([sQuery(id+"F0.wireOp",EDGE,"E25.0"),sQuery(id+"F0.wireOp",EDGE,"E25.1"),sQuery(id+"F0.wireOp",EDGE,"E25.2"),sQuery(id+"F0.wireOp",EDGE,"E25.3"),sQuery(id+"F0.wireOp",EDGE,"E25.4"),sQuery(id+"F0.wireOp",EDGE,"E25.5"),sQuery(id+"F0.wireOp",EDGE,"E25.6"),sQuery(id+"F0.wireOp",EDGE,"E25.7")])],"isStart":false})})});
            extrude(context, id + "F13", {"entities" : qUnion([Q0]), "operationType" : NewBodyOperationType.REMOVE, "endBound" : BoundingType.UP_TO_SURFACE, "endBoundEntityFace" : qUnion([Q1]), "depth" : 25 * mm});
        }
        {
            var Q0;
            Q0=makeQuery(id+"F3.boolean.opBoolean","COPY",EDGE,{"derivedFrom":makeQuery(id+"F3.opExtrude","CAP_EDGE",EDGE,{"disambiguationData":[OSD([sQuery(id+"F0.wireOp",EDGE,"E25.6")])],"isStart":false})});
            var Q1;
            Q1=makeQuery(id+"F8.boolean.opBoolean","INTERSECT",EDGE,{"derivedFrom":[makeQuery(id+"F5.opExtrude","SWEPT_FACE",FACE,{"disambiguationData":[OSD([sQuery(id+"F4.wireOp",EDGE,"E30")])]}),makeQuery(id+"F8.opExtrude","CAP_FACE",FACE,{"disambiguationData":[OSD([sQuery(id+"F7.wireOp",EDGE,"E67")])],"isStart":false})]});
            var Q2;
            Q2=makeQuery(id+"F8.boolean.opBoolean","INTERSECT",EDGE,{"disambiguationData":[OD(1.0)],"derivedFrom":[makeQuery(id+"F5.opExtrude","SWEPT_FACE",FACE,{"disambiguationData":[OSD([sQuery(id+"F4.wireOp",EDGE,"E30")])]}),makeQuery(id+"F8.opExtrude","SWEPT_FACE",FACE,{"disambiguationData":[OSD([sQuery(id+"F7.wireOp",EDGE,"E67")])]})]});
            var Q3;
            {var subQ0=sQuery(id+"F4.wireOp",EDGE,"E30");Q3=makeQuery(id+"F8.boolean.opBoolean","SPLIT",EDGE,{"disambiguationData":[TD([makeQuery(id+"F5.opExtrude","SWEPT_FACE",FACE,{"disambiguationData":[OSD([sQuery(id+"F4.wireOp",EDGE,"E35.filletArc")])]})])],"derivedFrom":makeQuery(id+"F5.opExtrude","CAP_EDGE",EDGE,{"disambiguationData":[OSD([subQ0])],"isStart":false})});}
            var Q4;
            {var subQ0=sQuery(id+"F0.wireOp",EDGE,"E25.7");var subQ1=sQuery(id+"F0.wireOp",EDGE,"E25.1");var subQ2=sQuery(id+"F0.wireOp",EDGE,"E25.6");var subQ3=sQuery(id+"F0.wireOp",EDGE,"E25.5");var subQ4=sQuery(id+"F0.wireOp",EDGE,"E25.4");var subQ5=sQuery(id+"F0.wireOp",EDGE,"E25.0");var subQ6=sQuery(id+"F0.wireOp",EDGE,"E25.2");var subQ7=sQuery(id+"F0.wireOp",EDGE,"E25.3");Q4=makeQuery(id+"F8.boolean.opBoolean","INTERSECT",EDGE,{"derivedFrom":[makeQuery(id+"F5.boolean.opBoolean","SPLIT",FACE,{"disambiguationData":[TD([makeQuery(id+"F2.opExtrude","SWEPT_FACE",FACE,{"disambiguationData":[OSD([subQ5])]})])],"derivedFrom":makeQuery(id+"F3.boolean.opBoolean","COPY",FACE,{"derivedFrom":makeQuery(id+"F3.opExtrude","CAP_FACE",FACE,{"disambiguationData":[OSD([subQ5,subQ1,subQ6,subQ7,subQ4,subQ3,subQ2,subQ0])],"isStart":false})})}),makeQuery(id+"F8.opExtrude","SWEPT_FACE",FACE,{"disambiguationData":[OSD([sQuery(id+"F7.wireOp",EDGE,"E67")])]})]});}
            var Q5;
            Q5=makeQuery(id+"F8.boolean.opBoolean","INTERSECT",EDGE,{"disambiguationData":[OD(0.0)],"derivedFrom":[makeQuery(id+"F5.opExtrude","SWEPT_FACE",FACE,{"disambiguationData":[OSD([sQuery(id+"F4.wireOp",EDGE,"E30")])]}),makeQuery(id+"F8.opExtrude","SWEPT_FACE",FACE,{"disambiguationData":[OSD([sQuery(id+"F7.wireOp",EDGE,"E67")])]})]});
            fillet(context, id + "F14", {"entities" : qUnion([Q0, Q1, Q2, Q3, Q4, Q5]), "radius" : 3 * mm, "tangentPropagation" : true, "allowEdgeOverflow" : false});
        }
        {
            var Q0;
            Q0=makeQuery(id+"F1.opExtrude","CAP_EDGE",EDGE,{"disambiguationData":[OSD([sQuery(id+"F0.wireOp",EDGE,"E1.bottom")])],"isStart":false});
            fillet(context, id + "F15", {"entities" : qUnion([Q0]), "radius" : 2 * mm, "tangentPropagation" : true, "allowEdgeOverflow" : false});
        }
        {
            var Q0;
            {var subQ0=sQuery(id+"F0.wireOp",EDGE,"E21.filletArc");var subQ1=sQuery(id+"F0.wireOp",EDGE,"E7");var subQ2=sQuery(id+"F0.wireOp",EDGE,"E6");var subQ3=sQuery(id+"F0.wireOp",EDGE,"E5");var subQ4=sQuery(id+"F0.wireOp",EDGE,"E4");var subQ5=sQuery(id+"F0.wireOp",EDGE,"E22.filletArc");var subQ6=sQuery(id+"F0.wireOp",EDGE,"E1.bottom");var subQ7=sQuery(id+"F0.wireOp",EDGE,"E1.right");var subQ8=sQuery(id+"F0.wireOp",EDGE,"E1.top");var subQ9=sQuery(id+"F0.wireOp",EDGE,"E1.left");var subQ10=sQuery(id+"F0.wireOp",EDGE,"E23.filletArc");var subQ11=sQuery(id+"F0.wireOp",EDGE,"E24.filletArc");Q0=makeQuery(id+"F2.boolean.opBoolean","SPLIT",FACE,{"disambiguationData":[TD([makeQuery(id+"F1.opExtrude","SWEPT_FACE",FACE,{"disambiguationData":[OSD([subQ6])]})])],"derivedFrom":makeQuery(id+"F1.opExtrude","CAP_FACE",FACE,{"disambiguationData":[OSD([subQ6,subQ8,subQ9,subQ7,subQ4,subQ3,subQ2,subQ1,subQ0,subQ5,subQ10,subQ11])],"isStart":true})});}
            var sketch = newSketch(context, id + "F16", { "sketchPlane" : qUnion([Q0])});
            skLineSegment(sketch, "E79.0", {"start": v(-70, 90) * mm, "end": v(70, 90) * mm});
            skLineSegment(sketch, "E79.1", {"start": v(80, -80) * mm, "end": v(80, 80) * mm});
            skArc(sketch, "E79.2", {"start": v(80, 80) * mm, "mid": v(77.07, 87.07) * mm, "end": v(70, 90) * mm});
            skArc(sketch, "E79.3", {"start": v(70, -90) * mm, "mid": v(77.07, -87.07) * mm, "end": v(80, -80) * mm});
            skLineSegment(sketch, "E79.4", {"start": v(-70, -90) * mm, "end": v(70, -90) * mm});
            skArc(sketch, "E79.5", {"start": v(-80, -80) * mm, "mid": v(-77.07, -87.07) * mm, "end": v(-70, -90) * mm});
            skLineSegment(sketch, "E79.6", {"start": v(-80, -80) * mm, "end": v(-80, 80) * mm});
            skArc(sketch, "E79.7", {"start": v(-70, 90) * mm, "mid": v(-77.07, 87.07) * mm, "end": v(-80, 80) * mm});
            skArc(sketch, "E79.8", {"start": v(56.15, 48.18) * mm, "mid": v(0, 67.5) * mm, "end": v(-56.15, 48.18) * mm});
            skCircle(sketch, "E79.9", {"center": v(-60, 67.5) * mm, "radius": 4 * mm});
            skArc(sketch, "E79.11", {"start": v(60, 40.3) * mm, "mid": v(58.99, 44.68) * mm, "end": v(56.15, 48.18) * mm});
            skLineSegment(sketch, "E79.12", {"start": v(60, 40.3) * mm, "end": v(60, -40.3) * mm});
            skArc(sketch, "E79.13", {"start": v(56.15, -48.18) * mm, "mid": v(58.99, -44.68) * mm, "end": v(60, -40.3) * mm});
            skArc(sketch, "E79.14", {"start": v(-56.15, -48.18) * mm, "mid": v(0, -67.5) * mm, "end": v(56.15, -48.18) * mm});
            skCircle(sketch, "E79.15", {"center": v(-60, -67.5) * mm, "radius": 4 * mm});
            skCircle(sketch, "E79.16", {"center": v(60, -67.5) * mm, "radius": 4 * mm});
            skArc(sketch, "E79.17", {"start": v(-60, -40.3) * mm, "mid": v(-58.99, -44.68) * mm, "end": v(-56.15, -48.18) * mm});
            skLineSegment(sketch, "E79.18", {"start": v(-60, 40.3) * mm, "end": v(-60, -40.3) * mm});
            skArc(sketch, "E79.19", {"start": v(-56.15, 48.18) * mm, "mid": v(-58.99, 44.68) * mm, "end": v(-60, 40.3) * mm});
            skLineSegment(sketch, "E80", {"start": v(0, 90) * mm, "end": v(0, 120) * mm, "construction": true});
            skCircle(sketch, "E81", {"center": v(0, 120) * mm, "radius": 6 * mm});
            skLineSegment(sketch, "E82", {"start": v(-33, 90) * mm, "end": v(-15, 108) * mm});
            skLineSegment(sketch, "E83", {"start": v(-15, 108) * mm, "end": v(-15, 120) * mm});
            skArc(sketch, "E84", {"start": v(15, 120) * mm, "mid": v(0, 135) * mm, "end": v(-15, 120) * mm});
            skLineSegment(sketch, "E85", {"start": v(15, 120) * mm, "end": v(15, 108) * mm});
            skLineSegment(sketch, "E86", {"start": v(15, 108) * mm, "end": v(33, 90) * mm});
            skLineSegment(sketch, "E87", {"start": v(-80, 0) * mm, "end": v(80, 0) * mm, "construction": true});
            skLineSegment(sketch, "E88", {"start": v(0, -90) * mm, "end": v(0, -120) * mm, "construction": true});
            skLineSegment(sketch, "E89", {"start": v(33, -90) * mm, "end": v(15, -108) * mm});
            skLineSegment(sketch, "E90", {"start": v(15, -108) * mm, "end": v(15, -120) * mm});
            skLineSegment(sketch, "E91", {"start": v(-33, -90) * mm, "end": v(-15, -108) * mm});
            skLineSegment(sketch, "E92", {"start": v(-15, -108) * mm, "end": v(-15, -120) * mm});
            skArc(sketch, "E93", {"start": v(-15, -120) * mm, "mid": v(0, -135) * mm, "end": v(15, -120) * mm});
            skCircle(sketch, "E94", {"center": v(0, -120) * mm, "radius": 6 * mm});
            skSolve(sketch);
        }
        {
            var Q0;
            Q0=makeQuery(id+"F16.imprint","IMPRINT",FACE,{"disambiguationData":[TD([[makeQuery(id+"F16.imprint","IMPRINT",EDGE,{"derivedFrom":sQuery(id+"F16.wireOp",EDGE,"E79.1")}),1.0]])]});
            var Q1;
            Q1=makeQuery(id+"F16.imprint","IMPRINT",FACE,{"disambiguationData":[TD([[makeQuery(id+"F16.imprint","IMPRINT",EDGE,{"derivedFrom":sQuery(id+"F16.wireOp",EDGE,"E81")}),-1.0]])]});
            var Q2;
            {var subQ1=sQuery(id+"F16.wireOp",EDGE,"E89");Q2=makeQuery(id+"F16.imprint","IMPRINT",FACE,{"disambiguationData":[TD([[makeQuery(id+"F16.imprint","IMPRINT",EDGE,{"derivedFrom":subQ1}),-1.0]])]});}
            var Q3;
            Q3=makeQuery(id+"F2.opExtrude","CAP_FACE",FACE,{"disambiguationData":[OSD([sQuery(id+"F0.wireOp",EDGE,"E12"),sQuery(id+"F0.wireOp",EDGE,"E13"),sQuery(id+"F0.wireOp",EDGE,"E14"),sQuery(id+"F0.wireOp",EDGE,"E15"),sQuery(id+"F0.wireOp",EDGE,"E17.filletArc"),sQuery(id+"F0.wireOp",EDGE,"E18.filletArc"),sQuery(id+"F0.wireOp",EDGE,"E19.filletArc"),sQuery(id+"F0.wireOp",EDGE,"E20.filletArc"),sQuery(id+"F0.wireOp",EDGE,"E25.0"),sQuery(id+"F0.wireOp",EDGE,"E25.1"),sQuery(id+"F0.wireOp",EDGE,"E25.2"),sQuery(id+"F0.wireOp",EDGE,"E25.3"),sQuery(id+"F0.wireOp",EDGE,"E25.4"),sQuery(id+"F0.wireOp",EDGE,"E25.5"),sQuery(id+"F0.wireOp",EDGE,"E25.6"),sQuery(id+"F0.wireOp",EDGE,"E25.7")])],"isStart":false});
            extrude(context, id + "F17", {"entities" : qUnion([Q0, Q1, Q2]), "surfaceOperationType" : NewSurfaceOperationType.ADD, "endBound" : BoundingType.UP_TO_SURFACE, "depth" : 25 * mm, "endBoundEntityFace" : qUnion([Q3]), "offsetDistance" : 25 * mm});
        }
    });
